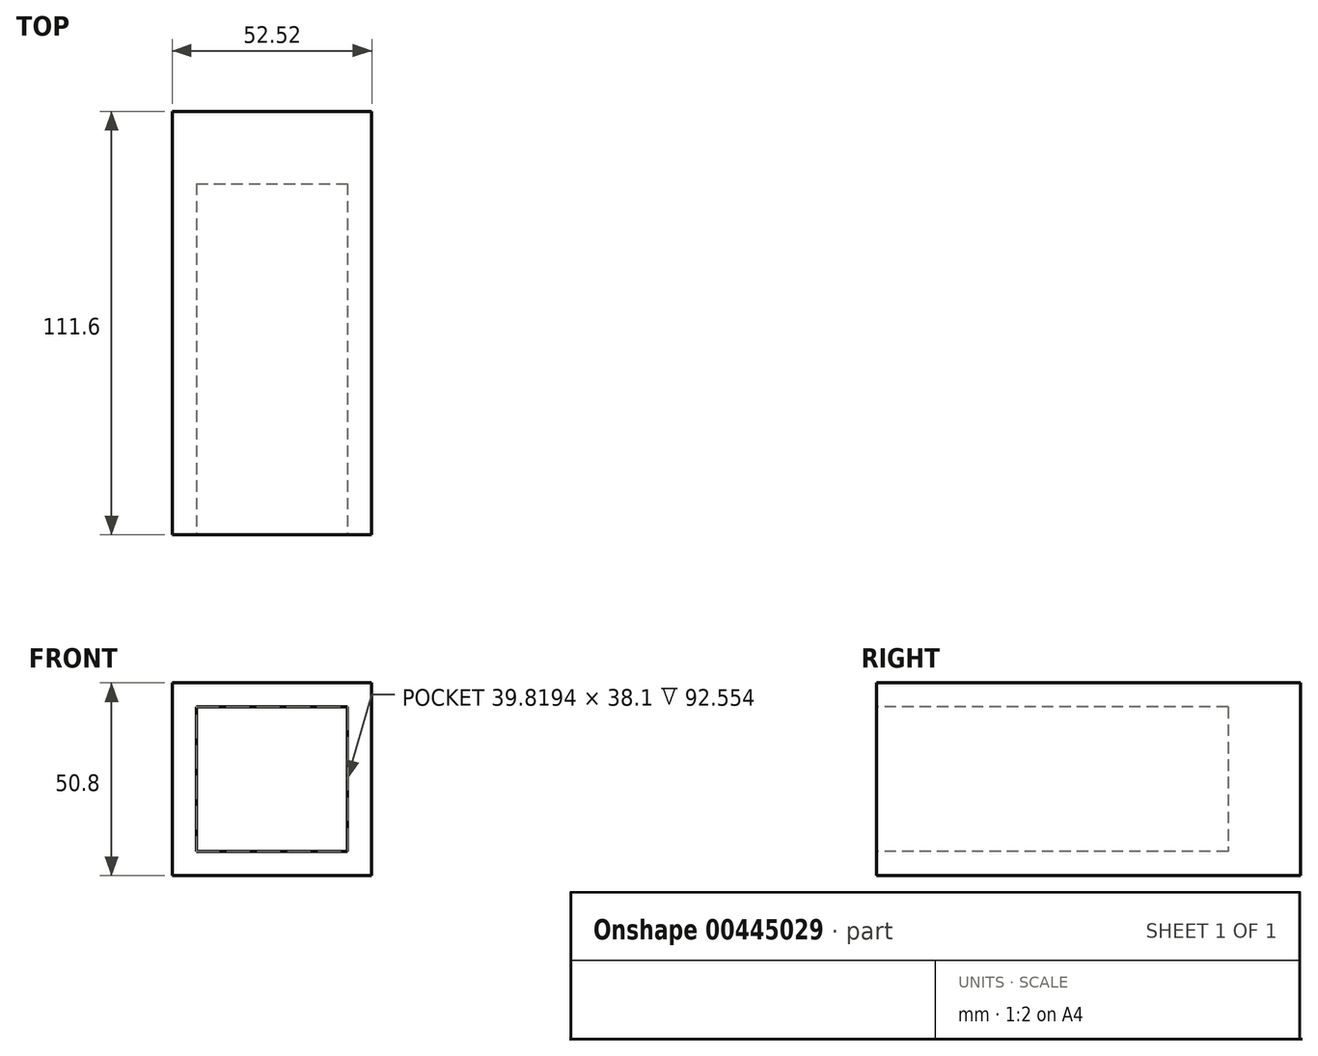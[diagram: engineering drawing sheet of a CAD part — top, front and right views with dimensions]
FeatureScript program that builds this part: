
annotation { "Feature Type Name" : "Feature", "Feature Type Description" : "" }
export const myFeature = defineFeature(function(context is Context, id is Id, definition is map)
    precondition{}
    {
        {
            var Q0;
            Q0=qCreatedBy(makeId("Top.planeOp"),FACE);
            var sketch = newSketch(context, id + "F0", { "sketchPlane" : qUnion([Q0])});
            skLineSegment(sketch, "E0.bottom", {"start": v(-24.31, 56.21) * mm, "end": v(28.2, 56.21) * mm});
            skLineSegment(sketch, "E0.top", {"start": v(-24.31, -55.4) * mm, "end": v(28.2, -55.4) * mm});
            skLineSegment(sketch, "E0.left", {"start": v(-24.31, 56.21) * mm, "end": v(-24.31, -55.4) * mm});
            skLineSegment(sketch, "E0.right", {"start": v(28.2, 56.21) * mm, "end": v(28.2, -55.4) * mm});
            skSolve(sketch);
        }
        {
            var Q0;
            Q0=makeQuery(id+"F0.imprint","IMPRINT",FACE,{"disambiguationData":[TD([[makeQuery(id+"F0.imprint","IMPRINT",EDGE,{"derivedFrom":sQuery(id+"F0.wireOp",EDGE,"E0.bottom")}),-1.0]])]});
            extrude(context, id + "F1", {"entities" : qUnion([Q0]), "depth" : 50.8 * mm});
        }
        {
            var Q0;
            Q0=makeQuery(id+"F1.opExtrude","SWEPT_FACE",FACE,{"disambiguationData":[OSD([sQuery(id+"F0.wireOp",EDGE,"E0.top")])]});
            shell(context, id + "F2", {"entities" : qUnion([Q0]), "thickness" : 6.35 * mm});
        }
        {
            var Q0;
            Q0=makeQuery(id+"F1.opExtrude","SWEPT_FACE",FACE,{"disambiguationData":[OSD([sQuery(id+"F0.wireOp",EDGE,"E0.bottom")])]});
            var Q1;
            Q1=makeQuery(id+"F2.opShell","OFFSET_FACE",FACE,{"disambiguationData":[OSD([sQuery(id+"F0.wireOp",EDGE,"E0.bottom")])]});
            extrude(context, id + "F3", {"entities" : qUnion([Q0, Q1]), "operationType" : NewBodyOperationType.ADD, "oppositeDirection" : true, "depth" : 12.7 * mm});
        }
    });
